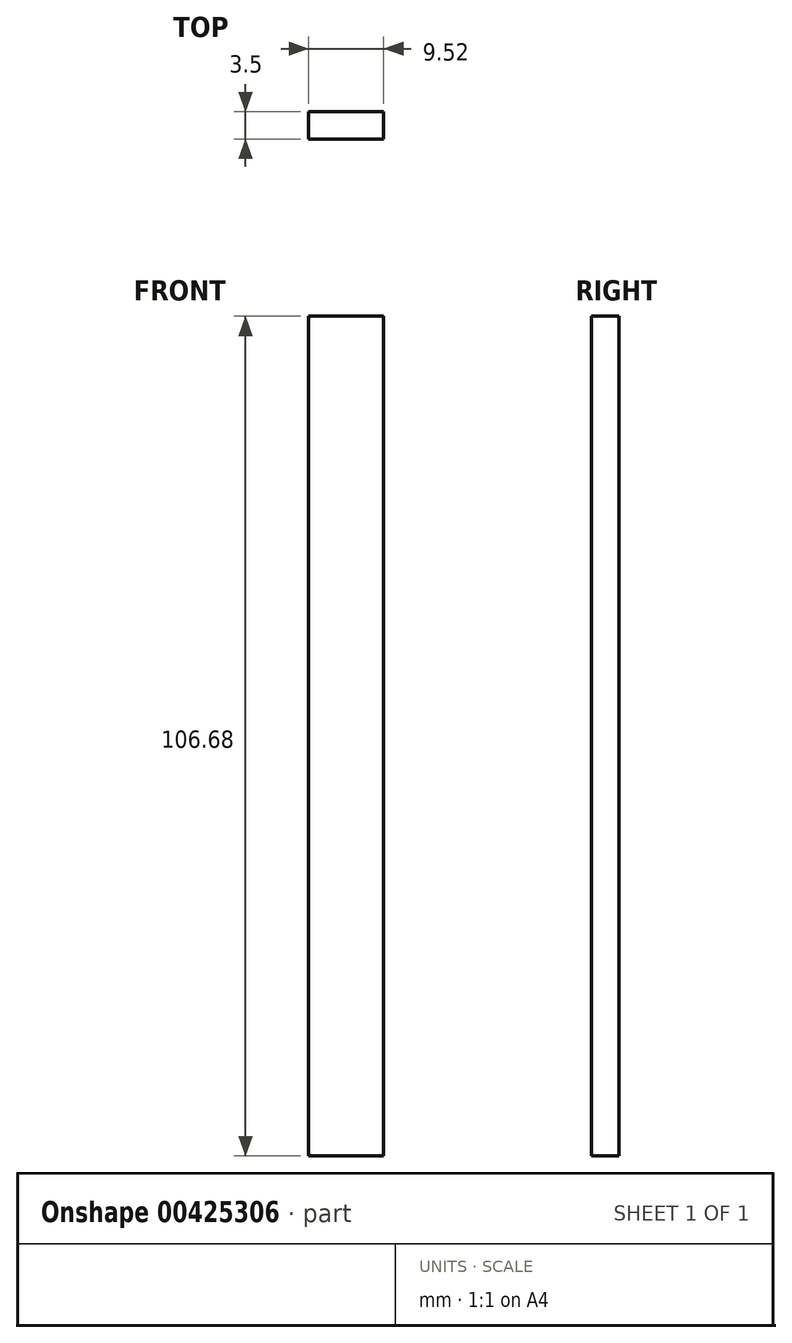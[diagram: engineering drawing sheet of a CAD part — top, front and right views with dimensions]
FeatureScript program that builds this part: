
annotation { "Feature Type Name" : "Feature", "Feature Type Description" : "" }
export const myFeature = defineFeature(function(context is Context, id is Id, definition is map)
    precondition{}
    {
        {
            var Q0;
            Q0=qCreatedBy(makeId("Front.planeOp"),FACE);
            var sketch = newSketch(context, id + "F0", { "sketchPlane" : qUnion([Q0])});
            skLineSegment(sketch, "E0.bottom", {"start": v(-36.01, 65.86) * mm, "end": v(-26.49, 65.86) * mm});
            skLineSegment(sketch, "E0.top", {"start": v(-36.01, -40.82) * mm, "end": v(-26.49, -40.82) * mm});
            skLineSegment(sketch, "E0.left", {"start": v(-36.01, 65.86) * mm, "end": v(-36.01, -40.82) * mm});
            skLineSegment(sketch, "E0.right", {"start": v(-26.49, 65.86) * mm, "end": v(-26.49, -40.82) * mm});
            skSolve(sketch);
        }
        {
            var Q0;
            Q0=makeQuery(id+"F0.imprint","IMPRINT",FACE,{"disambiguationData":[TD([[makeQuery(id+"F0.imprint","IMPRINT",EDGE,{"derivedFrom":sQuery(id+"F0.wireOp",EDGE,"E0.bottom")}),-1.0]])]});
            extrude(context, id + "F1", {"entities" : qUnion([Q0]), "depth" : 3.5 * mm, "offsetDistance" : 25.4 * mm});
        }
    });
